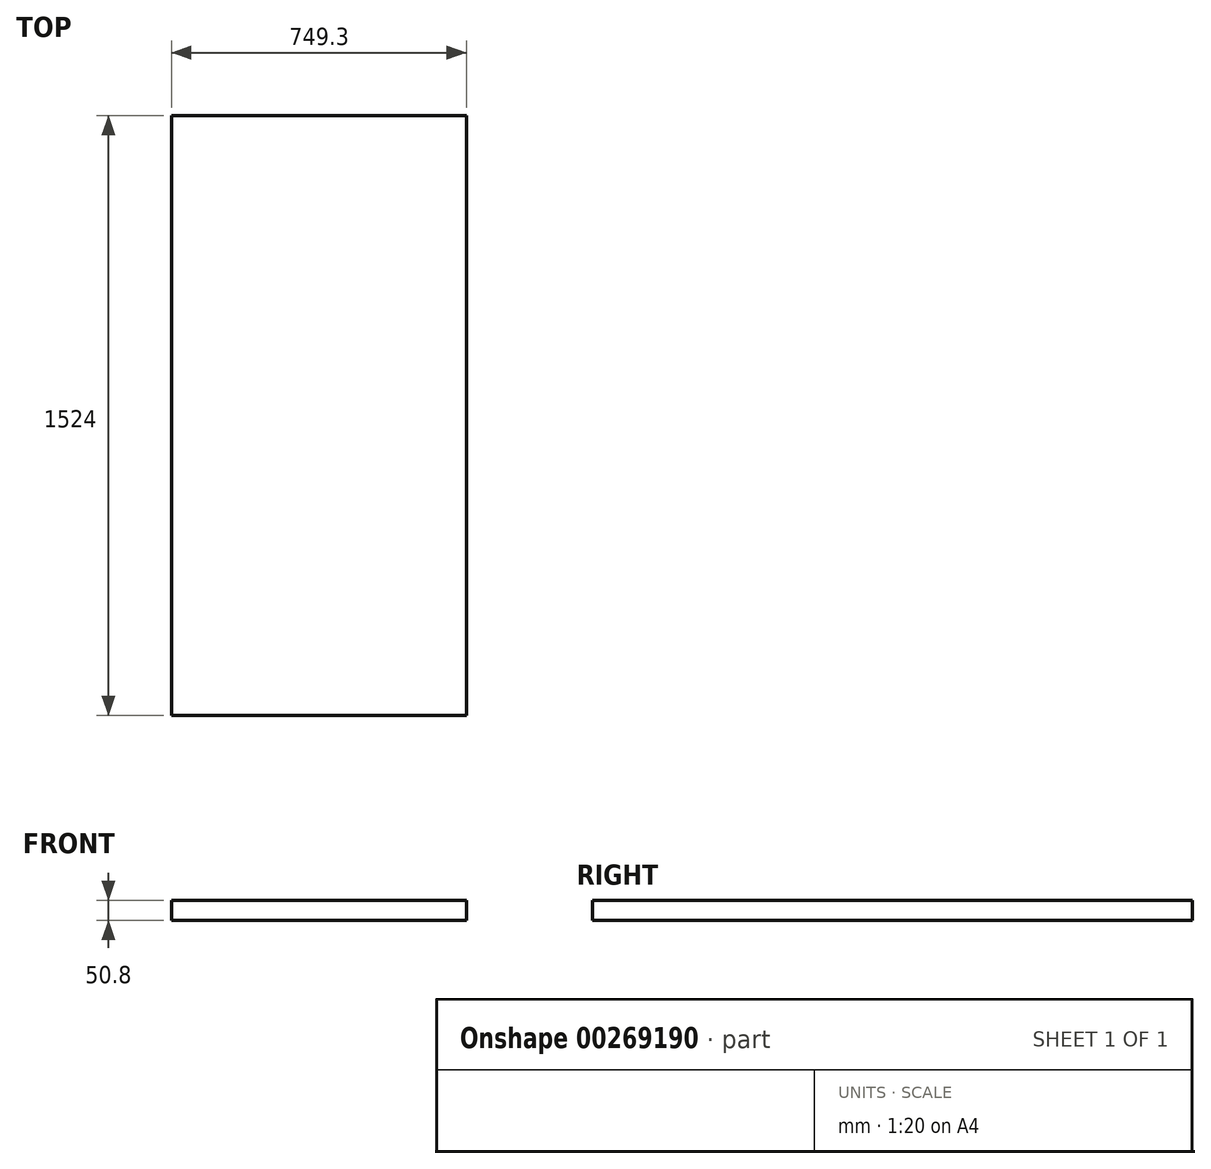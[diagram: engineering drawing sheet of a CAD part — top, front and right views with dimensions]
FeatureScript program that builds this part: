
annotation { "Feature Type Name" : "Feature", "Feature Type Description" : "" }
export const myFeature = defineFeature(function(context is Context, id is Id, definition is map)
    precondition{}
    {
        {
            var Q0;
            Q0=qCreatedBy(makeId("Top.planeOp"),FACE);
            var sketch = newSketch(context, id + "F0", { "sketchPlane" : qUnion([Q0])});
            skLineSegment(sketch, "E0.bottom", {"start": v(374.65, 762) * mm, "end": v(-374.65, 762) * mm});
            skLineSegment(sketch, "E0.top", {"start": v(374.65, -762) * mm, "end": v(-374.65, -762) * mm});
            skLineSegment(sketch, "E0.left", {"start": v(374.65, 762) * mm, "end": v(374.65, -762) * mm});
            skLineSegment(sketch, "E0.right", {"start": v(-374.65, 762) * mm, "end": v(-374.65, -762) * mm});
            skPoint(sketch, "E0.middle", {"position": v(0, 0) * mm});
            skSolve(sketch);
        }
        {
            var Q0;
            Q0 = qSketchRegion(id + "F0", true);
            extrude(context, id + "F1", {"entities" : qUnion([Q0]), "depth" : 50.8 * mm});
        }
    });
